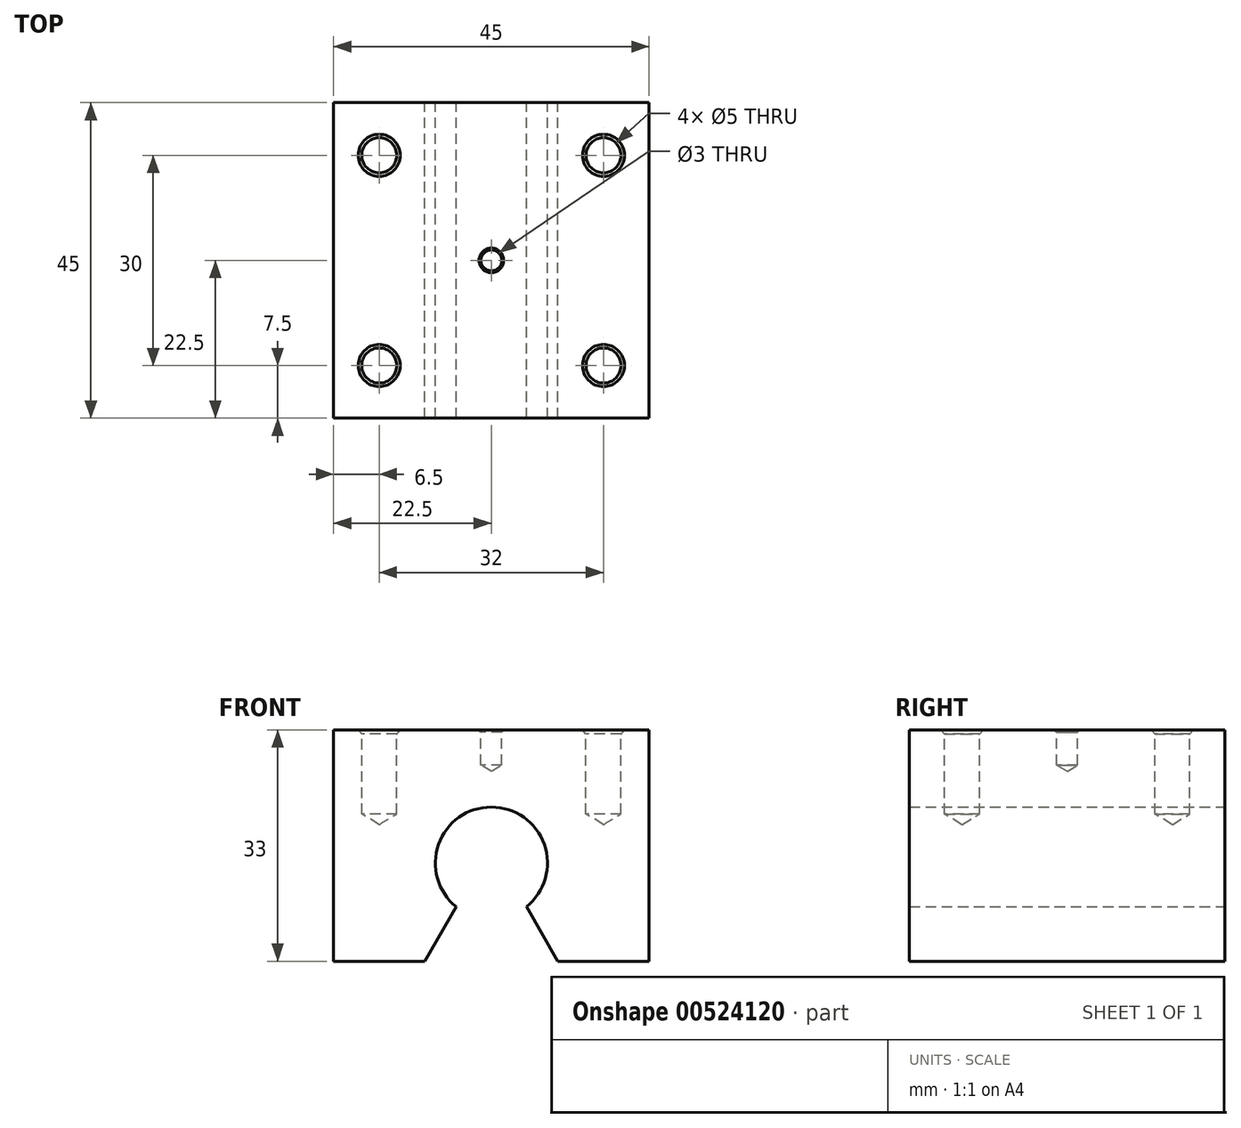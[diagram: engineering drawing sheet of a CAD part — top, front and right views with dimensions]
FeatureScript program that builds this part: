
annotation { "Feature Type Name" : "Feature", "Feature Type Description" : "" }
export const myFeature = defineFeature(function(context is Context, id is Id, definition is map)
    precondition{}
    {
        {
            var Q0;
            Q0=qCreatedBy(makeId("Front.planeOp"),FACE);
            var sketch = newSketch(context, id + "F0", { "sketchPlane" : qUnion([Q0])});
            skLineSegment(sketch, "E0", {"start": v(0, 0) * mm, "end": v(22.5, 0) * mm, "construction": true});
            skLineSegment(sketch, "E1", {"start": v(22.5, 0) * mm, "end": v(22.5, 33) * mm});
            skLineSegment(sketch, "E2", {"start": v(0, 0) * mm, "end": v(0, 50) * mm, "construction": true});
            skLineSegment(sketch, "E3", {"start": v(22.5, 33) * mm, "end": v(0, 33) * mm});
            skLineSegment(sketch, "E4.MirrorCS", {"start": v(-22.5, 33) * mm, "end": v(0, 33) * mm});
            skLineSegment(sketch, "E5.MirrorCS", {"start": v(-22.5, 0) * mm, "end": v(-22.5, 33) * mm});
            skLineSegment(sketch, "E6", {"start": v(22.5, 0) * mm, "end": v(9.5, 0) * mm});
            skLineSegment(sketch, "E7.MirrorCS", {"start": v(-22.5, 0) * mm, "end": v(-9.5, 0) * mm});
            skLineSegment(sketch, "E8", {"start": v(0, 33) * mm, "end": v(0, 14) * mm, "construction": true});
            skCircle(sketch, "E9", {"center": v(0, 14) * mm, "radius": 8 * mm});
            skLineSegment(sketch, "E10", {"start": v(9.5, 0) * mm, "end": v(5.02, 7.77) * mm});
            skLineSegment(sketch, "E11.MirrorCS", {"start": v(-9.5, 0) * mm, "end": v(-5.02, 7.77) * mm});
            skSolve(sketch);
        }
        {
            var Q0;
            Q0=makeQuery(id+"F0.imprint","IMPRINT",FACE,{"disambiguationData":[TD([[makeQuery(id+"F0.imprint","IMPRINT",EDGE,{"derivedFrom":sQuery(id+"F0.wireOp",EDGE,"E1")}),1.0]])]});
            extrude(context, id + "F1", {"entities" : qUnion([Q0]), "depth" : 45 * mm, "offsetDistance" : 25 * mm});
        }
        {
            var Q0;
            Q0=qCreatedBy(makeId("Top.planeOp"),FACE);
            var sketch = newSketch(context, id + "F2", { "sketchPlane" : qUnion([Q0])});
            skLineSegment(sketch, "E12", {"start": v(0, 0) * mm, "end": v(0, -45) * mm, "construction": true});
            skLineSegment(sketch, "E13", {"start": v(0, 0) * mm, "end": v(22.5, 0) * mm, "construction": true});
            skLineSegment(sketch, "E14", {"start": v(0, 0) * mm, "end": v(0, -22.5) * mm, "construction": true});
            skPoint(sketch, "E15", {"position": v(0, -22.5) * mm});
            skCircle(sketch, "E16", {"center": v(0, -22.5) * mm, "radius": 2 * mm});
            skLineSegment(sketch, "E17", {"start": v(0, -22.5) * mm, "end": v(0, -7.5) * mm, "construction": true});
            skLineSegment(sketch, "E18", {"start": v(0, -7.5) * mm, "end": v(16, -7.5) * mm, "construction": true});
            skPoint(sketch, "E19", {"position": v(16, -7.5) * mm});
            skLineSegment(sketch, "E20", {"start": v(16, -7.5) * mm, "end": v(16, -37.5) * mm, "construction": true});
            skPoint(sketch, "E21", {"position": v(16, -37.5) * mm});
            skCircle(sketch, "E22", {"center": v(16, -7.5) * mm, "radius": 2.5 * mm});
            skCircle(sketch, "E23", {"center": v(16, -37.5) * mm, "radius": 2.5 * mm});
            skCircle(sketch, "E24.MirrorC", {"center": v(-16, -37.5) * mm, "radius": 2.5 * mm});
            skCircle(sketch, "E25.MirrorC", {"center": v(-16, -7.5) * mm, "radius": 2.5 * mm});
            skSolve(sketch);
        }
        {
            var Q0;
            Q0=qCreatedBy(makeId("Top.planeOp"),FACE);
            cPlane(context, id + "F3", {"entities" : qUnion([Q0]), "cplaneType" : CPlaneType.OFFSET, "offset" : 33 * mm, "width" : 150 * mm, "height" : 150 * mm});
        }
        {
            var Q0;
            Q0=qCreatedBy(id+"F3.planeOp",FACE);
            var sketch = newSketch(context, id + "F4", { "sketchPlane" : qUnion([Q0])});
            skLineSegment(sketch, "E26", {"start": v(0, 0) * mm, "end": v(0, -45) * mm, "construction": true});
            skLineSegment(sketch, "E27", {"start": v(0, 0) * mm, "end": v(0, -22.5) * mm, "construction": true});
            skCircle(sketch, "E28", {"center": v(0, -22.5) * mm, "radius": 1.5 * mm});
            skLineSegment(sketch, "E29", {"start": v(0, -22.5) * mm, "end": v(0, -7.5) * mm, "construction": true});
            skLineSegment(sketch, "E30", {"start": v(0, -7.5) * mm, "end": v(16, -7.5) * mm, "construction": true});
            skPoint(sketch, "E31", {"position": v(16, -7.5) * mm});
            skCircle(sketch, "E32", {"center": v(16, -7.5) * mm, "radius": 2.5 * mm});
            skLineSegment(sketch, "E33", {"start": v(16, -7.5) * mm, "end": v(16, -37.5) * mm, "construction": true});
            skPoint(sketch, "E34", {"position": v(16, -37.5) * mm});
            skCircle(sketch, "E35", {"center": v(16, -37.5) * mm, "radius": 2.5 * mm});
            skCircle(sketch, "E36.MirrorC", {"center": v(-16, -7.5) * mm, "radius": 2.5 * mm});
            skCircle(sketch, "E37.MirrorC", {"center": v(-16, -37.5) * mm, "radius": 2.5 * mm});
            skSolve(sketch);
        }
        {
            var Q0;
            Q0=sQuery(id+"F4.wireOp",VERTEX,"E36.MirrorC.center");
            var Q1;
            Q1=sQuery(id+"F4.wireOp",VERTEX,"E37.MirrorC.center");
            var Q2;
            Q2=sQuery(id+"F4.wireOp",VERTEX,"E34");
            var Q3;
            Q3=sQuery(id+"F4.wireOp",VERTEX,"E31");
            var Q4;
            Q4=makeQuery(id+"F1.opExtrude","SWEPT_BODY",BODY,{"disambiguationData":[OSD([sQuery(id+"F0.wireOp",EDGE,"E1"),sQuery(id+"F0.wireOp",EDGE,"E3"),sQuery(id+"F0.wireOp",EDGE,"E4.MirrorCS"),sQuery(id+"F0.wireOp",EDGE,"E5.MirrorCS"),sQuery(id+"F0.wireOp",EDGE,"E6"),sQuery(id+"F0.wireOp",EDGE,"E7.MirrorCS"),sQuery(id+"F0.wireOp",EDGE,"E9"),sQuery(id+"F0.wireOp",EDGE,"E10"),sQuery(id+"F0.wireOp",EDGE,"E11.MirrorCS")])]});
            hole(context, id + "F5", {"style" : HoleStyle.C_SINK, "endStyle" : HoleEndStyle.BLIND, "holeDiameter" : 5 * mm, "cSinkDiameter" : 6 * mm, "cSinkAngle" : 80 * degree, "holeDepth" : 12 * mm, "isTappedThrough" : true, "tappedDepth" : 12 * mm, "tapClearance" : 3, "startFromSketch" : true, "locations" : qUnion([Q0, Q1, Q2, Q3]), "scope" : qUnion([Q4])});
        }
        {
            var Q0;
            Q0=sQuery(id+"F4.wireOp",VERTEX,"E28.center");
            var Q1;
            Q1=makeQuery(id+"F1.opExtrude","SWEPT_BODY",BODY,{"disambiguationData":[OSD([sQuery(id+"F0.wireOp",EDGE,"E1"),sQuery(id+"F0.wireOp",EDGE,"E3"),sQuery(id+"F0.wireOp",EDGE,"E4.MirrorCS"),sQuery(id+"F0.wireOp",EDGE,"E5.MirrorCS"),sQuery(id+"F0.wireOp",EDGE,"E6"),sQuery(id+"F0.wireOp",EDGE,"E7.MirrorCS"),sQuery(id+"F0.wireOp",EDGE,"E9"),sQuery(id+"F0.wireOp",EDGE,"E10"),sQuery(id+"F0.wireOp",EDGE,"E11.MirrorCS")])]});
            hole(context, id + "F6", {"style" : HoleStyle.C_SINK, "endStyle" : HoleEndStyle.BLIND, "holeDiameter" : 3 * mm, "cSinkDiameter" : 3.5 * mm, "cSinkAngle" : 80 * degree, "holeDepth" : 5 * mm, "isTappedThrough" : true, "tappedDepth" : 12 * mm, "tapClearance" : 3, "startFromSketch" : true, "locations" : qUnion([Q0]), "scope" : qUnion([Q1])});
        }
    });
